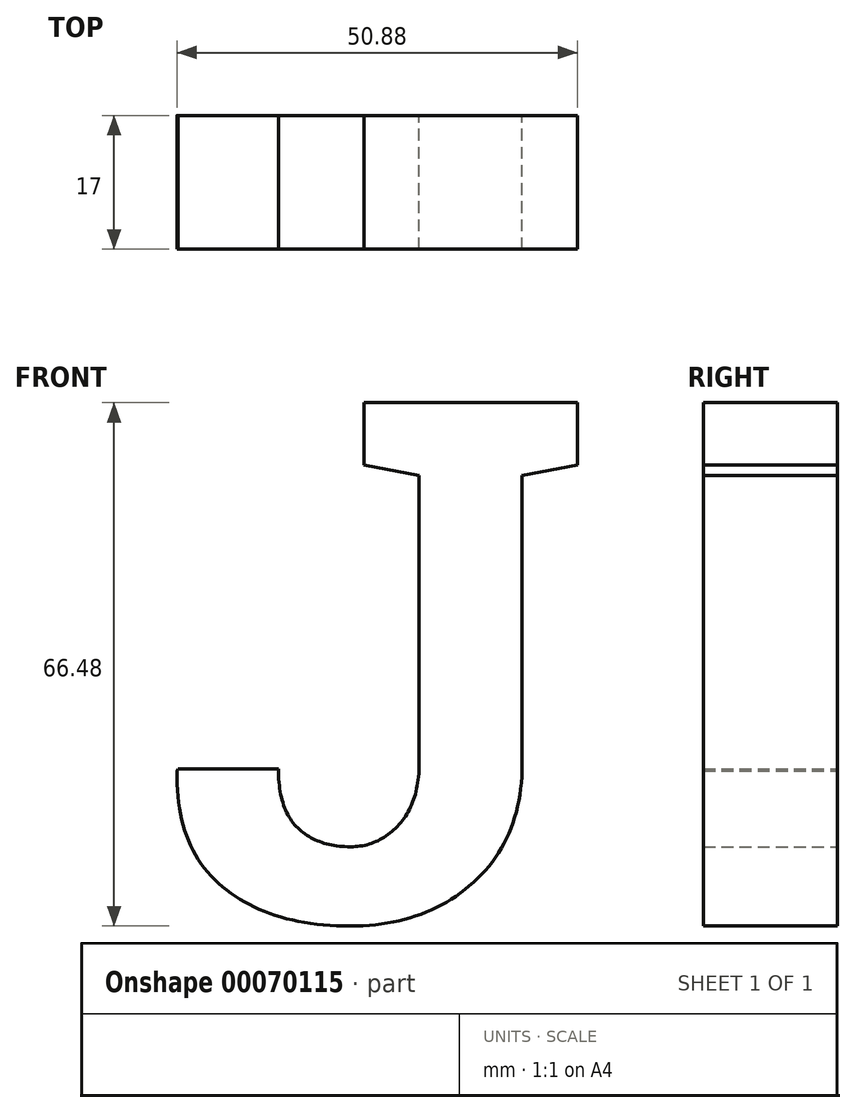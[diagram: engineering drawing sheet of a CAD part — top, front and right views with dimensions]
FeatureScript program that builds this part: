
annotation { "Feature Type Name" : "Feature", "Feature Type Description" : "" }
export const myFeature = defineFeature(function(context is Context, id is Id, definition is map)
    precondition{}
    {
        {
            var Q0;
            Q0=qCreatedBy(makeId("Front.planeOp"),FACE);
            var sketch = newSketch(context, id + "F0", { "sketchPlane" : qUnion([Q0])});
            skText(sketch, "E0", { "text": "J", "fontName": "RobotoSlab-Bold.ttf"});
            const initialGuessF0  = {"E0": [0.0125, 0.00403, 1, 0, 0.06637]};
            skSetInitialGuess(sketch, initialGuessF0);
            skSolve(sketch);
        }
        {
            var Q0;
            Q0=makeQuery(id+"F0.imprint","IMPRINT",FACE,{"disambiguationData":[TD([[makeQuery(id+"F0.imprint","IMPRINT",EDGE,{"derivedFrom":sQuery(id+"F0.wireOp",EDGE,"E0.sketch_text.stroke-0")}),-1.0]])]});
            extrude(context, id + "F1", {"entities" : qUnion([Q0]), "depth" : 17 * mm});
        }
    });
